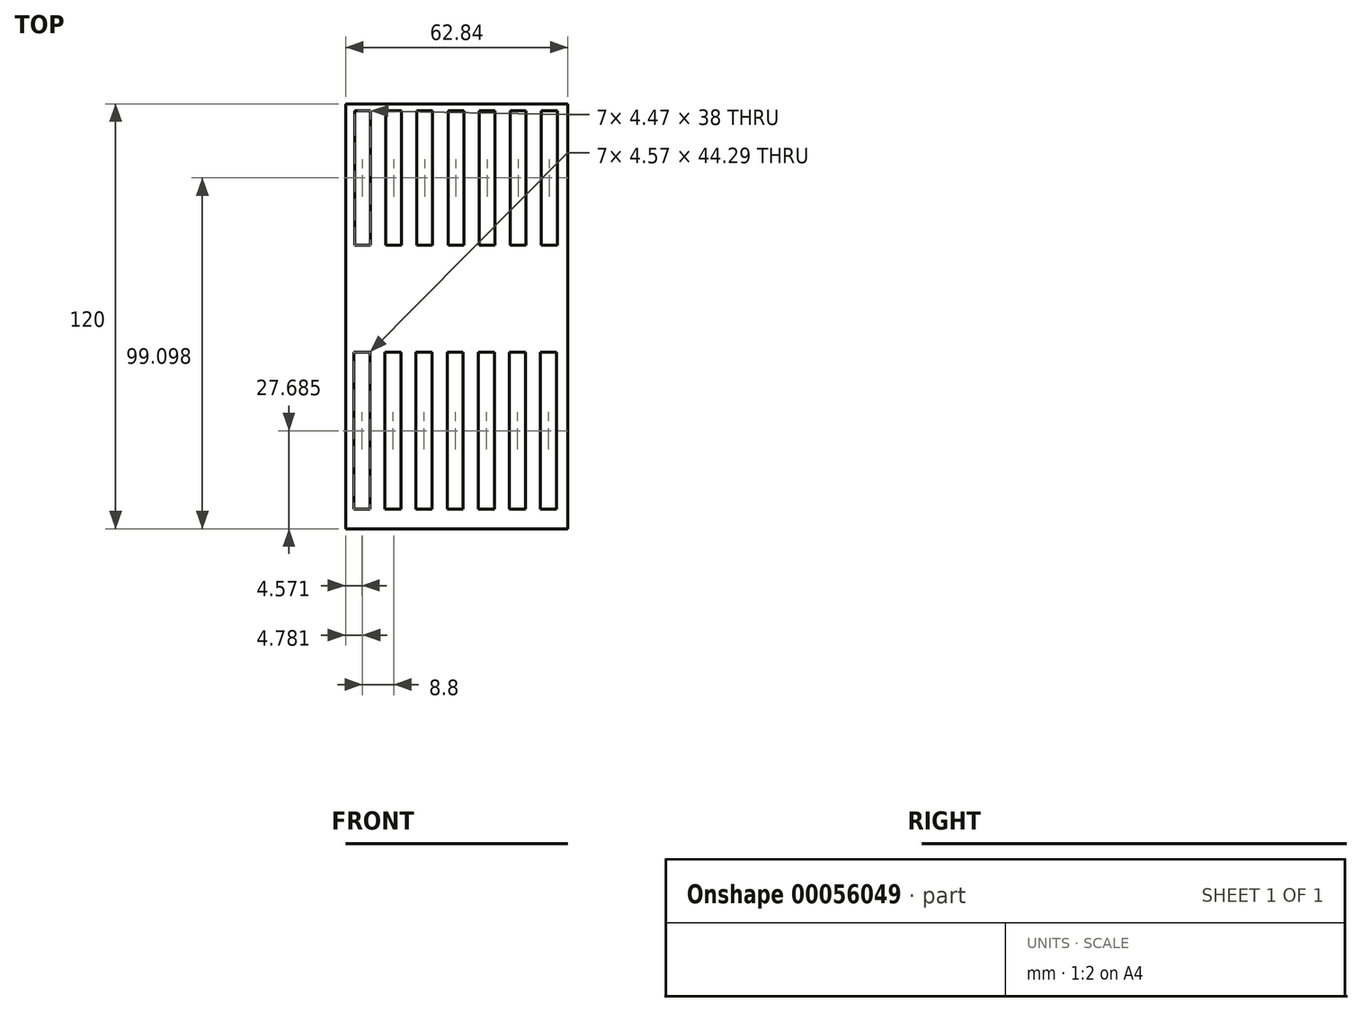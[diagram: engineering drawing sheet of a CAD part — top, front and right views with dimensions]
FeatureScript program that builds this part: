
annotation { "Feature Type Name" : "Feature", "Feature Type Description" : "" }
export const myFeature = defineFeature(function(context is Context, id is Id, definition is map)
    precondition{}
    {
        {
            var Q0;
            Q0=qCreatedBy(makeId("Top.planeOp"),FACE);
            var sketch = newSketch(context, id + "F0", { "sketchPlane" : qUnion([Q0])});
            skLineSegment(sketch, "E0.bottom", {"start": v(-48.75, -27.76) * mm, "end": v(14.09, -27.76) * mm});
            skLineSegment(sketch, "E0.top", {"start": v(-48.75, 92.24) * mm, "end": v(14.09, 92.24) * mm});
            skLineSegment(sketch, "E0.left", {"start": v(-48.75, -27.76) * mm, "end": v(-48.75, 92.24) * mm});
            skLineSegment(sketch, "E0.right", {"start": v(14.09, -27.76) * mm, "end": v(14.09, 92.24) * mm});
            skSolve(sketch);
        }
        {
            var Q0;
            Q0=makeQuery(id+"F0.imprint","IMPRINT",FACE,{"disambiguationData":[TD([[makeQuery(id+"F0.imprint","IMPRINT",EDGE,{"derivedFrom":sQuery(id+"F0.wireOp",EDGE,"E0.bottom")}),1.0]])]});
            extrude(context, id + "F1", {"entities" : qUnion([Q0]), "depth" : 1 / 203.2 * mm});
        }
        {
            var Q0;
            Q0=makeQuery(id+"F1.opExtrude","CAP_FACE",FACE,{"disambiguationData":[OSD([sQuery(id+"F0.wireOp",EDGE,"E0.bottom"),sQuery(id+"F0.wireOp",EDGE,"E0.top"),sQuery(id+"F0.wireOp",EDGE,"E0.left"),sQuery(id+"F0.wireOp",EDGE,"E0.right")])],"isStart":false});
            var sketch = newSketch(context, id + "F2", { "sketchPlane" : qUnion([Q0])});
            skLineSegment(sketch, "E1.bottom", {"start": v(-46.2, 90.34) * mm, "end": v(-41.73, 90.34) * mm});
            skLineSegment(sketch, "E1.top", {"start": v(-46.2, 52.34) * mm, "end": v(-41.73, 52.34) * mm});
            skLineSegment(sketch, "E1.left", {"start": v(-46.2, 90.34) * mm, "end": v(-46.2, 52.34) * mm});
            skLineSegment(sketch, "E1.right", {"start": v(-41.73, 90.34) * mm, "end": v(-41.73, 52.34) * mm});
            skLineSegment(sketch, "E2.1.0.0", {"start": v(-37.4, 90.34) * mm, "end": v(-32.93, 90.34) * mm});
            skLineSegment(sketch, "E2.1.0.1", {"start": v(-37.4, 52.34) * mm, "end": v(-32.93, 52.34) * mm});
            skLineSegment(sketch, "E2.1.0.2", {"start": v(-37.4, 90.34) * mm, "end": v(-37.4, 52.34) * mm});
            skLineSegment(sketch, "E2.1.0.3", {"start": v(-32.93, 90.34) * mm, "end": v(-32.93, 52.34) * mm});
            skLineSegment(sketch, "E2.2.0.0", {"start": v(-28.6, 90.34) * mm, "end": v(-24.13, 90.34) * mm});
            skLineSegment(sketch, "E2.2.0.1", {"start": v(-28.6, 52.34) * mm, "end": v(-24.13, 52.34) * mm});
            skLineSegment(sketch, "E2.2.0.2", {"start": v(-28.6, 90.34) * mm, "end": v(-28.6, 52.34) * mm});
            skLineSegment(sketch, "E2.2.0.3", {"start": v(-24.13, 90.34) * mm, "end": v(-24.13, 52.34) * mm});
            skLineSegment(sketch, "E2.3.0.0", {"start": v(-19.8, 90.34) * mm, "end": v(-15.33, 90.34) * mm});
            skLineSegment(sketch, "E2.3.0.1", {"start": v(-19.8, 52.34) * mm, "end": v(-15.33, 52.34) * mm});
            skLineSegment(sketch, "E2.3.0.2", {"start": v(-19.8, 90.34) * mm, "end": v(-19.8, 52.34) * mm});
            skLineSegment(sketch, "E2.3.0.3", {"start": v(-15.33, 90.34) * mm, "end": v(-15.33, 52.34) * mm});
            skLineSegment(sketch, "E2.4.0.0", {"start": v(-11, 90.34) * mm, "end": v(-6.53, 90.34) * mm});
            skLineSegment(sketch, "E2.4.0.1", {"start": v(-11, 52.34) * mm, "end": v(-6.53, 52.34) * mm});
            skLineSegment(sketch, "E2.4.0.2", {"start": v(-11, 90.34) * mm, "end": v(-11, 52.34) * mm});
            skLineSegment(sketch, "E2.4.0.3", {"start": v(-6.53, 90.34) * mm, "end": v(-6.53, 52.34) * mm});
            skLineSegment(sketch, "E2.5.0.0", {"start": v(-2.2, 90.34) * mm, "end": v(2.27, 90.34) * mm});
            skLineSegment(sketch, "E2.5.0.1", {"start": v(-2.2, 52.34) * mm, "end": v(2.27, 52.34) * mm});
            skLineSegment(sketch, "E2.5.0.2", {"start": v(-2.2, 90.34) * mm, "end": v(-2.2, 52.34) * mm});
            skLineSegment(sketch, "E2.5.0.3", {"start": v(2.27, 90.34) * mm, "end": v(2.27, 52.34) * mm});
            skLineSegment(sketch, "E2.6.0.0", {"start": v(6.6, 90.34) * mm, "end": v(11.07, 90.34) * mm});
            skLineSegment(sketch, "E2.6.0.1", {"start": v(6.6, 52.34) * mm, "end": v(11.07, 52.34) * mm});
            skLineSegment(sketch, "E2.6.0.2", {"start": v(6.6, 90.34) * mm, "end": v(6.6, 52.34) * mm});
            skLineSegment(sketch, "E2.6.0.3", {"start": v(11.07, 90.34) * mm, "end": v(11.07, 52.34) * mm});
            skLineSegment(sketch, "E2.direction1", {"start": v(-46.2, 90.34) * mm, "end": v(-37.4, 90.34) * mm, "construction": true});
            skSolve(sketch);
        }
        {
            var Q0;
            Q0=makeQuery(id+"F2.imprint","IMPRINT",FACE,{"disambiguationData":[TD([[makeQuery(id+"F2.imprint","IMPRINT",EDGE,{"derivedFrom":sQuery(id+"F2.wireOp",EDGE,"E1.bottom")}),1.0]])]});
            var sketch = newSketch(context, id + "F3", { "sketchPlane" : qUnion([Q0])});
            skLineSegment(sketch, "E3.bottom", {"start": v(-46.46, 22.07) * mm, "end": v(-41.9, 22.07) * mm});
            skLineSegment(sketch, "E3.top", {"start": v(-46.46, -22.22) * mm, "end": v(-41.9, -22.22) * mm});
            skLineSegment(sketch, "E3.left", {"start": v(-46.46, 22.07) * mm, "end": v(-46.46, -22.22) * mm});
            skLineSegment(sketch, "E3.right", {"start": v(-41.9, 22.07) * mm, "end": v(-41.9, -22.22) * mm});
            skLineSegment(sketch, "E4.1.0.0", {"start": v(-37.66, 22.07) * mm, "end": v(-33.1, 22.07) * mm});
            skLineSegment(sketch, "E4.1.0.1", {"start": v(-37.66, -22.22) * mm, "end": v(-33.1, -22.22) * mm});
            skLineSegment(sketch, "E4.1.0.2", {"start": v(-37.66, 22.07) * mm, "end": v(-37.66, -22.22) * mm});
            skLineSegment(sketch, "E4.1.0.3", {"start": v(-33.1, 22.07) * mm, "end": v(-33.1, -22.22) * mm});
            skLineSegment(sketch, "E4.2.0.0", {"start": v(-28.86, 22.07) * mm, "end": v(-24.3, 22.07) * mm});
            skLineSegment(sketch, "E4.2.0.1", {"start": v(-28.86, -22.22) * mm, "end": v(-24.3, -22.22) * mm});
            skLineSegment(sketch, "E4.2.0.2", {"start": v(-28.86, 22.07) * mm, "end": v(-28.86, -22.22) * mm});
            skLineSegment(sketch, "E4.2.0.3", {"start": v(-24.3, 22.07) * mm, "end": v(-24.3, -22.22) * mm});
            skLineSegment(sketch, "E4.3.0.0", {"start": v(-20.06, 22.07) * mm, "end": v(-15.5, 22.07) * mm});
            skLineSegment(sketch, "E4.3.0.1", {"start": v(-20.06, -22.22) * mm, "end": v(-15.5, -22.22) * mm});
            skLineSegment(sketch, "E4.3.0.2", {"start": v(-20.06, 22.07) * mm, "end": v(-20.06, -22.22) * mm});
            skLineSegment(sketch, "E4.3.0.3", {"start": v(-15.5, 22.07) * mm, "end": v(-15.5, -22.22) * mm});
            skLineSegment(sketch, "E4.4.0.0", {"start": v(-11.26, 22.07) * mm, "end": v(-6.7, 22.07) * mm});
            skLineSegment(sketch, "E4.4.0.1", {"start": v(-11.26, -22.22) * mm, "end": v(-6.7, -22.22) * mm});
            skLineSegment(sketch, "E4.4.0.2", {"start": v(-11.26, 22.07) * mm, "end": v(-11.26, -22.22) * mm});
            skLineSegment(sketch, "E4.4.0.3", {"start": v(-6.7, 22.07) * mm, "end": v(-6.7, -22.22) * mm});
            skLineSegment(sketch, "E4.5.0.0", {"start": v(-2.46, 22.07) * mm, "end": v(2.1, 22.07) * mm});
            skLineSegment(sketch, "E4.5.0.1", {"start": v(-2.46, -22.22) * mm, "end": v(2.1, -22.22) * mm});
            skLineSegment(sketch, "E4.5.0.2", {"start": v(-2.46, 22.07) * mm, "end": v(-2.46, -22.22) * mm});
            skLineSegment(sketch, "E4.5.0.3", {"start": v(2.1, 22.07) * mm, "end": v(2.1, -22.22) * mm});
            skLineSegment(sketch, "E4.6.0.0", {"start": v(6.34, 22.07) * mm, "end": v(10.9, 22.07) * mm});
            skLineSegment(sketch, "E4.6.0.1", {"start": v(6.34, -22.22) * mm, "end": v(10.9, -22.22) * mm});
            skLineSegment(sketch, "E4.6.0.2", {"start": v(6.34, 22.07) * mm, "end": v(6.34, -22.22) * mm});
            skLineSegment(sketch, "E4.6.0.3", {"start": v(10.9, 22.07) * mm, "end": v(10.9, -22.22) * mm});
            skLineSegment(sketch, "E4.direction1", {"start": v(-46.46, 22.07) * mm, "end": v(-37.66, 22.07) * mm, "construction": true});
            skSolve(sketch);
        }
        {
            var Q0;
            Q0=makeQuery(id+"F2.imprint","IMPRINT",FACE,{"disambiguationData":[TD([[makeQuery(id+"F2.imprint","IMPRINT",EDGE,{"derivedFrom":sQuery(id+"F2.wireOp",EDGE,"E2.2.0.0")}),-1.0]])]});
            var Q1;
            Q1=makeQuery(id+"F2.imprint","IMPRINT",FACE,{"disambiguationData":[TD([[makeQuery(id+"F2.imprint","IMPRINT",EDGE,{"derivedFrom":sQuery(id+"F2.wireOp",EDGE,"E1.bottom")}),-1.0]])]});
            var Q2;
            Q2=makeQuery(id+"F2.imprint","IMPRINT",FACE,{"disambiguationData":[TD([[makeQuery(id+"F2.imprint","IMPRINT",EDGE,{"derivedFrom":sQuery(id+"F2.wireOp",EDGE,"E2.1.0.0")}),-1.0]])]});
            var Q3;
            Q3=makeQuery(id+"F2.imprint","IMPRINT",FACE,{"disambiguationData":[TD([[makeQuery(id+"F2.imprint","IMPRINT",EDGE,{"derivedFrom":sQuery(id+"F2.wireOp",EDGE,"E2.4.0.0")}),-1.0]])]});
            var Q4;
            Q4=makeQuery(id+"F2.imprint","IMPRINT",FACE,{"disambiguationData":[TD([[makeQuery(id+"F2.imprint","IMPRINT",EDGE,{"derivedFrom":sQuery(id+"F2.wireOp",EDGE,"E2.5.0.0")}),-1.0]])]});
            var Q5;
            Q5=makeQuery(id+"F2.imprint","IMPRINT",FACE,{"disambiguationData":[TD([[makeQuery(id+"F2.imprint","IMPRINT",EDGE,{"derivedFrom":sQuery(id+"F2.wireOp",EDGE,"E2.6.0.0")}),-1.0]])]});
            var Q6;
            Q6=makeQuery(id+"F3.imprint","IMPRINT",FACE,{"disambiguationData":[TD([[makeQuery(id+"F3.imprint","IMPRINT",EDGE,{"derivedFrom":makeQuery(id+"F2.imprint","IMPRINT",EDGE,{"derivedFrom":sQuery(id+"F2.wireOp",EDGE,"E2.3.0.0")})}),-1.0]])]});
            var Q7;
            Q7=makeQuery(id+"F3.imprint","IMPRINT",FACE,{"disambiguationData":[TD([[makeQuery(id+"F3.imprint","IMPRINT",EDGE,{"derivedFrom":sQuery(id+"F3.wireOp",EDGE,"E4.5.0.0")}),-1.0]])]});
            var Q8;
            Q8=makeQuery(id+"F3.imprint","IMPRINT",FACE,{"disambiguationData":[TD([[makeQuery(id+"F3.imprint","IMPRINT",EDGE,{"derivedFrom":sQuery(id+"F3.wireOp",EDGE,"E4.4.0.0")}),-1.0]])]});
            var Q9;
            Q9=makeQuery(id+"F3.imprint","IMPRINT",FACE,{"disambiguationData":[TD([[makeQuery(id+"F3.imprint","IMPRINT",EDGE,{"derivedFrom":sQuery(id+"F3.wireOp",EDGE,"E4.3.0.0")}),-1.0]])]});
            var Q10;
            Q10=makeQuery(id+"F3.imprint","IMPRINT",FACE,{"disambiguationData":[TD([[makeQuery(id+"F3.imprint","IMPRINT",EDGE,{"derivedFrom":sQuery(id+"F3.wireOp",EDGE,"E4.2.0.0")}),-1.0]])]});
            var Q11;
            Q11=makeQuery(id+"F3.imprint","IMPRINT",FACE,{"disambiguationData":[TD([[makeQuery(id+"F3.imprint","IMPRINT",EDGE,{"derivedFrom":sQuery(id+"F3.wireOp",EDGE,"E4.1.0.0")}),-1.0]])]});
            var Q12;
            Q12=makeQuery(id+"F3.imprint","IMPRINT",FACE,{"disambiguationData":[TD([[makeQuery(id+"F3.imprint","IMPRINT",EDGE,{"derivedFrom":sQuery(id+"F3.wireOp",EDGE,"E3.bottom")}),-1.0]])]});
            var Q13;
            Q13=makeQuery(id+"F3.imprint","IMPRINT",FACE,{"disambiguationData":[TD([[makeQuery(id+"F3.imprint","IMPRINT",EDGE,{"derivedFrom":sQuery(id+"F3.wireOp",EDGE,"E4.6.0.0")}),-1.0]])]});
            extrude(context, id + "F4", {"entities" : qUnion([Q0, Q1, Q2, Q3, Q4, Q5, Q6, Q7, Q8, Q9, Q10, Q11, Q12, Q13]), "operationType" : NewBodyOperationType.REMOVE, "oppositeDirection" : true, "depth" : 1 * mm});
        }
    });
